# Revit family: Módulo Endereçável para Pressurização de Escadas MPRES2-E ILUMAC
name_source: partatom
category: Dispositivos de alarme de incêndio
units: mm (PartAtom-declared; Revit-internal decimal feet)

## family parameters
Com base no plano de trabalho = Não
Compartilhado = Não
Corte com vazios quando carregada = Não
Cota do conector redondo = Utilizar diâmetro
Manter orientação da anotação = Não
Número OmniClass = 23.80.30.11.17
Ponto de cálculo do ambiente = Não
Sempre na vertical = Sim
Tipo de parte = Normal
Título OmniClass = Distribution Boards and Control Panels

## types (1)
- MPRES2-E
    Capacidade das saídas = 30V @ 500mA (carga resistiva CA/CC)
    Correntes de consumo = 3,5mA @ 24Vcc em supervisão.
32mA @ 24Vcc em pulso acionamento (3s)
5mA @ 24Vcc em alarme
    Código = 02259
    Descrição = Módulo Endereçável para Pressurização de Escadas MPRES2-E
    Dimensões (AxLxP) = 60x100x28mm
    Dispositivo na entrada = 1 à 4 detectores (limitados à corrente de 1mA)*
    Elevação padrão = 0 mm  [stored 0 ft]
    Endereços programáveis = 1 à 500
    Fabricante = ILUMAC
    Fixação = Caixa de sobrepor com bornes de conexão
    Grau de proteção = IP20 (uso interno)
    Impedância do drive de comunicação = 47K Ohms
    Material da caixa = Caixa plástica ABS cinza
    Modelo = MPRES2-E
    Normas técnicas aplicáveis = NBR 17240 | ISO 7240-18 | NBR 14880
    Peso = 80g
    Protocolo de comunicação = ALF-500 (proprietário)
    Temperatura de operação = 0 à 50oC
    Tensão de operação = 22 à 28Vcc
    Tensão nominal = 24Vcc
    Tipo de entrada = 1 laço convencional supervisionado
    Tipo de saída = 1 saída contato-seco pulsante SPDT-NA.
1 saída contato-seco pulsante SPDT-NF.
    Umidade relativa = 0 à 95% (sem condensação)

note: [stored X ft] marks values corroborated as IEEE doubles in the binary element streams (Revit-internal decimal feet)
